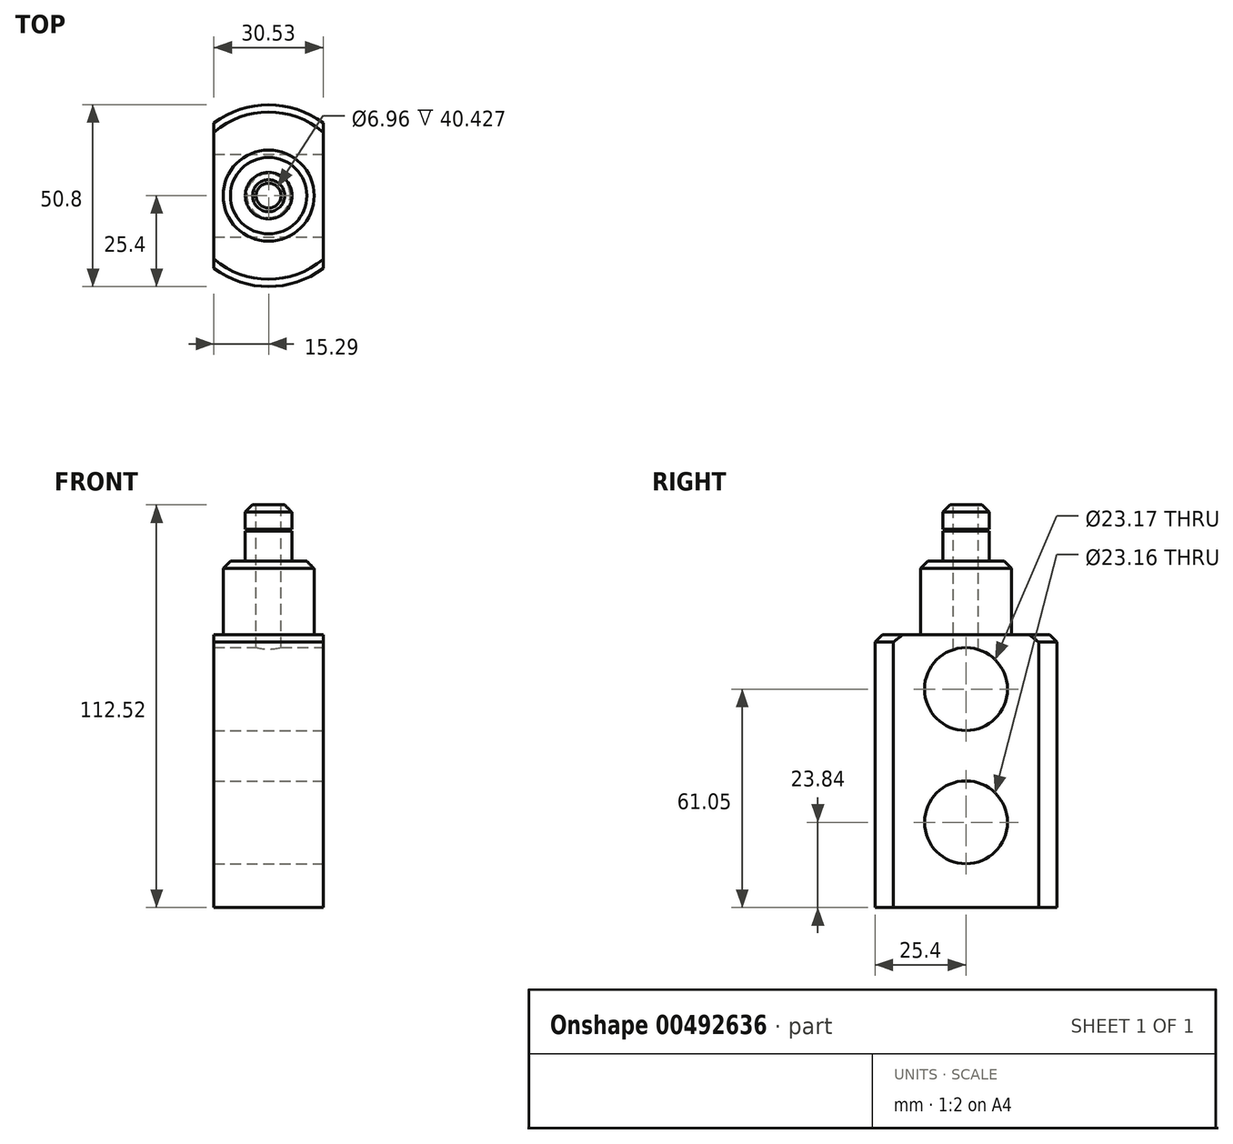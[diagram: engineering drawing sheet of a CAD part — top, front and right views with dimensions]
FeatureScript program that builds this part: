
annotation { "Feature Type Name" : "Feature", "Feature Type Description" : "" }
export const myFeature = defineFeature(function(context is Context, id is Id, definition is map)
    precondition{}
    {
        {
            var Q0;
            Q0=qCreatedBy(makeId("Top.planeOp"),FACE);
            var sketch = newSketch(context, id + "F0", { "sketchPlane" : qUnion([Q0])});
            skCircle(sketch, "E0", {"center": v(0, 0) * mm, "radius": 25.4 * mm});
            skSolve(sketch);
        }
        {
            var Q0;
            Q0 = qSketchRegion(id + "F0", true);
            extrude(context, id + "F1", {"entities" : qUnion([Q0]), "depth" : 76.2 * mm});
        }
        {
            var Q0;
            Q0=makeQuery(id+"F1.opExtrude","CAP_FACE",FACE,{"disambiguationData":[OSD([sQuery(id+"F0.wireOp",EDGE,"E0")])],"isStart":false});
            var sketch = newSketch(context, id + "F2", { "sketchPlane" : qUnion([Q0])});
            skCircle(sketch, "E1", {"center": v(0, 0) * mm, "radius": 12.71 * mm});
            skSolve(sketch);
        }
        {
            var Q0;
            Q0 = qSketchRegion(id + "F2", true);
            extrude(context, id + "F3", {"entities" : qUnion([Q0]), "operationType" : NewBodyOperationType.ADD, "depth" : 20.57 * mm});
        }
        {
            var Q0;
            Q0=makeQuery(id+"F3.opExtrude","CAP_FACE",FACE,{"disambiguationData":[OSD([sQuery(id+"F2.wireOp",EDGE,"E1")])],"isStart":false});
            var sketch = newSketch(context, id + "F4", { "sketchPlane" : qUnion([Q0])});
            skCircle(sketch, "E2", {"center": v(0, 0) * mm, "radius": 6.5 * mm});
            skSolve(sketch);
        }
        {
            var Q0;
            Q0 = qSketchRegion(id + "F4", true);
            extrude(context, id + "F5", {"entities" : qUnion([Q0]), "operationType" : NewBodyOperationType.ADD, "depth" : 8.38 * mm});
        }
        {
            var Q0;
            Q0=makeQuery(id+"F5.opExtrude","CAP_FACE",FACE,{"disambiguationData":[OSD([sQuery(id+"F4.wireOp",EDGE,"E2")])],"isStart":false});
            var sketch = newSketch(context, id + "F6", { "sketchPlane" : qUnion([Q0])});
            skCircle(sketch, "E3", {"center": v(0, 0) * mm, "radius": 5.53 * mm});
            skSolve(sketch);
        }
        {
            var Q0;
            Q0 = qSketchRegion(id + "F6", true);
            extrude(context, id + "F7", {"entities" : qUnion([Q0]), "operationType" : NewBodyOperationType.ADD, "oppositeDirection" : true, "depth" : 0.36 * mm});
        }
        {
            var Q0;
            Q0=makeQuery(id+"F5.opExtrude","CAP_FACE",FACE,{"disambiguationData":[OSD([sQuery(id+"F4.wireOp",EDGE,"E2")])],"isStart":false});
            var sketch = newSketch(context, id + "F8", { "sketchPlane" : qUnion([Q0])});
            skCircle(sketch, "E4", {"center": v(0, 0) * mm, "radius": 6.07 * mm});
            skSolve(sketch);
        }
        {
            var Q0;
            Q0 = qSketchRegion(id + "F8", true);
            extrude(context, id + "F9", {"entities" : qUnion([Q0]), "operationType" : NewBodyOperationType.ADD, "depth" : 0.56 * mm});
        }
        {
            var Q0;
            Q0=makeQuery(id+"F9.opExtrude","CAP_FACE",FACE,{"disambiguationData":[OSD([sQuery(id+"F8.wireOp",EDGE,"E4")])],"isStart":false});
            var sketch = newSketch(context, id + "F10", { "sketchPlane" : qUnion([Q0])});
            skCircle(sketch, "E5", {"center": v(0, 0) * mm, "radius": 6.5 * mm});
            skSolve(sketch);
        }
        {
            var Q0;
            Q0 = qSketchRegion(id + "F10", true);
            extrude(context, id + "F11", {"entities" : qUnion([Q0]), "operationType" : NewBodyOperationType.ADD, "depth" : 6.8 * mm});
        }
        {
            var Q0;
            Q0=makeQuery(id+"F1.opExtrude","CAP_FACE",FACE,{"disambiguationData":[OSD([sQuery(id+"F0.wireOp",EDGE,"E0")])],"isStart":false});
            var sketch = newSketch(context, id + "F12", { "sketchPlane" : qUnion([Q0])});
            skLineSegment(sketch, "E6.bottom", {"start": v(-15.29, 23.07) * mm, "end": v(-28.12, 23.07) * mm});
            skLineSegment(sketch, "E6.top", {"start": v(-15.29, -23.28) * mm, "end": v(-28.12, -23.28) * mm});
            skLineSegment(sketch, "E6.left", {"start": v(-15.29, 23.07) * mm, "end": v(-15.29, -23.28) * mm});
            skLineSegment(sketch, "E6.right", {"start": v(-28.12, 23.07) * mm, "end": v(-28.12, -23.28) * mm});
            skSolve(sketch);
        }
        {
            var Q0;
            Q0 = qSketchRegion(id + "F12", true);
            extrude(context, id + "F13", {"entities" : qUnion([Q0]), "operationType" : NewBodyOperationType.REMOVE, "oppositeDirection" : true, "depth" : 254 * mm});
        }
        {
            var Q0;
            Q0=makeQuery(id+"F1.opExtrude","CAP_FACE",FACE,{"disambiguationData":[OSD([sQuery(id+"F0.wireOp",EDGE,"E0")])],"isStart":false});
            var sketch = newSketch(context, id + "F14", { "sketchPlane" : qUnion([Q0])});
            skLineSegment(sketch, "E7.bottom", {"start": v(15.24, 25.28) * mm, "end": v(30.64, 25.28) * mm});
            skLineSegment(sketch, "E7.top", {"start": v(15.24, -26.4) * mm, "end": v(30.64, -26.4) * mm});
            skLineSegment(sketch, "E7.left", {"start": v(15.24, 25.28) * mm, "end": v(15.24, -26.4) * mm});
            skLineSegment(sketch, "E7.right", {"start": v(30.64, 25.28) * mm, "end": v(30.64, -26.4) * mm});
            skSolve(sketch);
        }
        {
            var Q0;
            Q0 = qSketchRegion(id + "F14", true);
            extrude(context, id + "F15", {"entities" : qUnion([Q0]), "operationType" : NewBodyOperationType.REMOVE, "oppositeDirection" : true, "depth" : 254 * mm});
        }
        {
            var Q0;
            Q0=makeQuery(id+"F15.boolean.opBoolean","COPY",FACE,{"derivedFrom":makeQuery(id+"F15.opExtrude","SWEPT_FACE",FACE,{"disambiguationData":[OSD([sQuery(id+"F14.wireOp",EDGE,"E7.left")])]})});
            var sketch = newSketch(context, id + "F16", { "sketchPlane" : qUnion([Q0])});
            skCircle(sketch, "E8", {"center": v(0, 61.05) * mm, "radius": 11.59 * mm});
            skCircle(sketch, "E9", {"center": v(0, 17.22) * mm, "radius": 11.58 * mm});
            skSolve(sketch);
        }
        {
            var Q0;
            Q0=makeQuery(id+"F16.imprint","IMPRINT",FACE,{"disambiguationData":[TD([[makeQuery(id+"F16.imprint","IMPRINT",EDGE,{"derivedFrom":sQuery(id+"F16.wireOp",EDGE,"E8")}),1.0]])]});
            var Q1;
            Q1=sQuery(id+"F16.wireOp",EDGE,"E8");
            extrude(context, id + "F17", {"entities" : qUnion([Q0]), "operationType" : NewBodyOperationType.REMOVE, "surfaceEntities" : qUnion([Q1]), "oppositeDirection" : true, "depth" : 254 * mm});
        }
        {
            var Q0;
            Q0=makeQuery(id+"F15.boolean.opBoolean","COPY",FACE,{"derivedFrom":makeQuery(id+"F15.opExtrude","SWEPT_FACE",FACE,{"disambiguationData":[OSD([sQuery(id+"F14.wireOp",EDGE,"E7.left")])]})});
            var sketch = newSketch(context, id + "F18", { "sketchPlane" : qUnion([Q0])});
            skCircle(sketch, "E10", {"center": v(0, 23.84) * mm, "radius": 11.58 * mm});
            skSolve(sketch);
        }
        {
            var Q0;
            Q0=makeQuery(id+"F18.imprint","IMPRINT",FACE,{"disambiguationData":[TD([[makeQuery(id+"F18.imprint","IMPRINT",EDGE,{"derivedFrom":sQuery(id+"F18.wireOp",EDGE,"E10")}),1.0]])]});
            var Q1;
            Q1=sQuery(id+"F18.wireOp",EDGE,"E10");
            extrude(context, id + "F19", {"entities" : qUnion([Q0]), "operationType" : NewBodyOperationType.REMOVE, "surfaceEntities" : qUnion([Q1]), "oppositeDirection" : true, "depth" : 254 * mm});
        }
        {
            var Q0;
            Q0=makeQuery(id+"F15.boolean.opBoolean","SPLIT",EDGE,{"disambiguationData":[OD(0.0)],"derivedFrom":makeQuery(id+"F1.opExtrude","CAP_EDGE",EDGE,{"disambiguationData":[OSD([sQuery(id+"F0.wireOp",EDGE,"E0")])],"isStart":false})});
            chamfer(context, id + "F20", {"entities" : qUnion([Q0]), "width" : 2.03 * mm, "tangentPropagation" : true});
        }
        {
            var Q0;
            Q0=makeQuery(id+"F15.boolean.opBoolean","SPLIT",EDGE,{"disambiguationData":[OD(1.0)],"derivedFrom":makeQuery(id+"F1.opExtrude","CAP_EDGE",EDGE,{"disambiguationData":[OSD([sQuery(id+"F0.wireOp",EDGE,"E0")])],"isStart":false})});
            chamfer(context, id + "F21", {"entities" : qUnion([Q0]), "width" : 2.03 * mm, "tangentPropagation" : true});
        }
        {
            var Q0;
            Q0=makeQuery(id+"F3.opExtrude","CAP_EDGE",EDGE,{"disambiguationData":[OSD([sQuery(id+"F2.wireOp",EDGE,"E1")])],"isStart":false});
            chamfer(context, id + "F22", {"entities" : qUnion([Q0]), "width" : 2.03 * mm, "tangentPropagation" : true});
        }
        {
            var Q0;
            Q0=makeQuery(id+"F11.opExtrude","CAP_EDGE",EDGE,{"disambiguationData":[OSD([sQuery(id+"F10.wireOp",EDGE,"E5")])],"isStart":false});
            chamfer(context, id + "F23", {"entities" : qUnion([Q0]), "width" : 2.03 * mm, "tangentPropagation" : true});
        }
        {
            var Q0;
            Q0=makeQuery(id+"F11.opExtrude","CAP_FACE",FACE,{"disambiguationData":[OSD([sQuery(id+"F10.wireOp",EDGE,"E5")])],"isStart":false});
            var sketch = newSketch(context, id + "F24", { "sketchPlane" : qUnion([Q0])});
            skCircle(sketch, "E11", {"center": v(0, 0) * mm, "radius": 3.48 * mm});
            skSolve(sketch);
        }
        {
            var Q0;
            Q0 = qSketchRegion(id + "F24", true);
            extrude(context, id + "F25", {"entities" : qUnion([Q0]), "operationType" : NewBodyOperationType.REMOVE, "oppositeDirection" : true, "depth" : 50.8 * mm});
        }
    });
